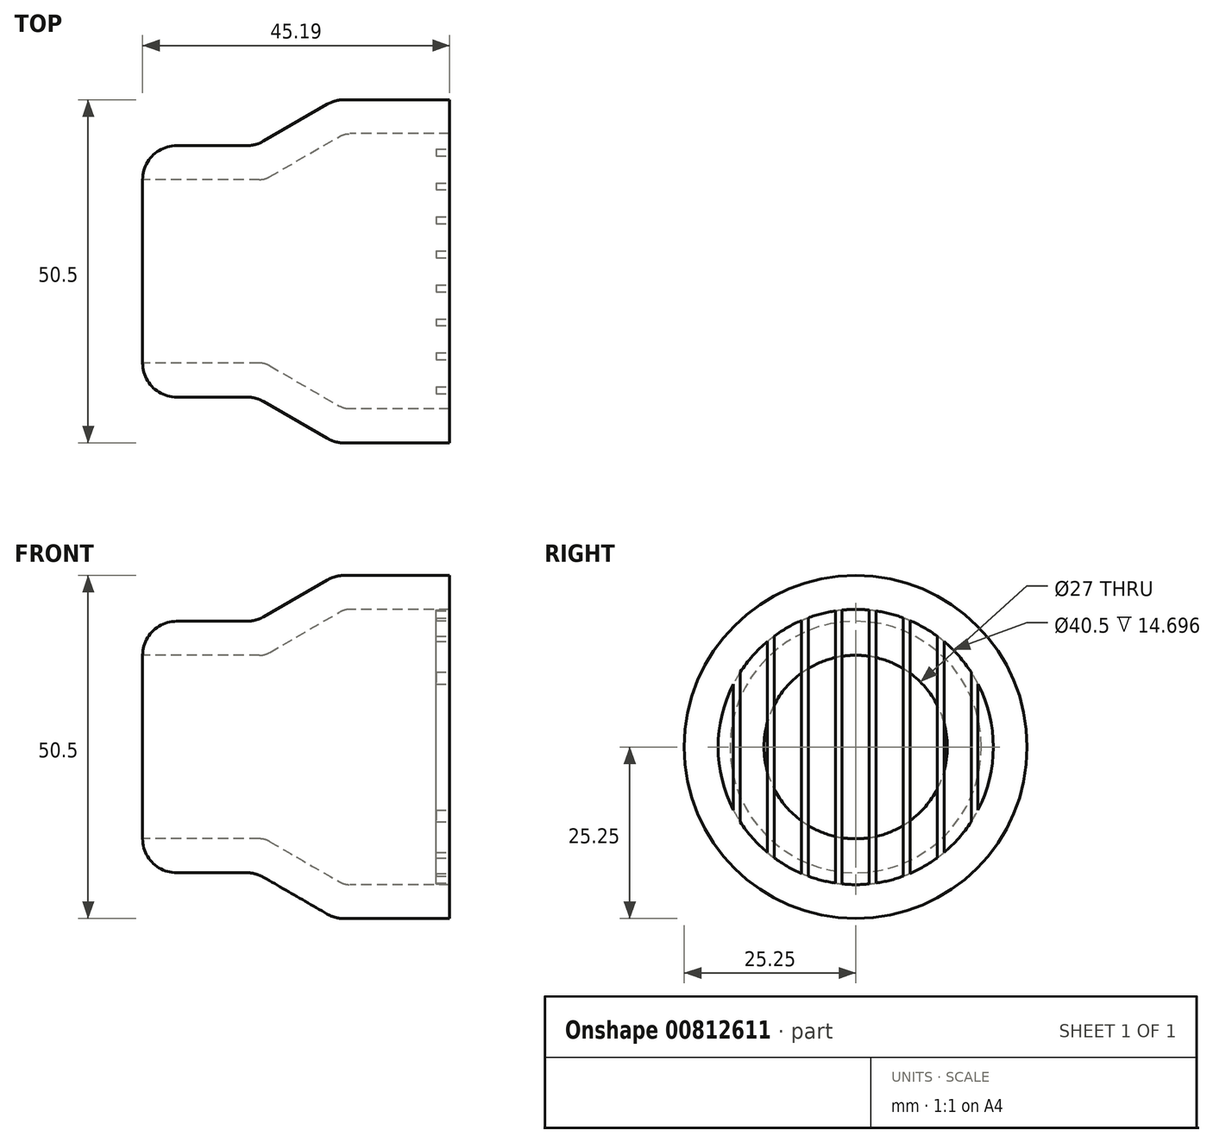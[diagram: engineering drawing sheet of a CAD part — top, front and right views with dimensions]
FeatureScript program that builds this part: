
annotation { "Feature Type Name" : "Feature", "Feature Type Description" : "" }
export const myFeature = defineFeature(function(context is Context, id is Id, definition is map)
    precondition{}
    {
        {
            var Q0;
            Q0=qCreatedBy(makeId("Top.planeOp"),FACE);
            var sketch = newSketch(context, id + "F0", { "sketchPlane" : qUnion([Q0])});
            skLineSegment(sketch, "E0", {"start": v(-18, 13.5) * mm, "end": v(0, 13.5) * mm});
            skLineSegment(sketch, "E1", {"start": v(0, 13.5) * mm, "end": v(11.7, 20.25) * mm});
            skLineSegment(sketch, "E2", {"start": v(11.7, 20.25) * mm, "end": v(25.2, 20.25) * mm});
            skLineSegment(sketch, "E3.0", {"start": v(10.35, 25.25) * mm, "end": v(25.2, 25.25) * mm});
            skLineSegment(sketch, "E3.1", {"start": v(-1.34, 18.5) * mm, "end": v(10.35, 25.25) * mm});
            skLineSegment(sketch, "E3.2", {"start": v(-18, 18.5) * mm, "end": v(-1.34, 18.5) * mm});
            skLineSegment(sketch, "E4", {"start": v(-18, 13.5) * mm, "end": v(-18, 18.5) * mm});
            skLineSegment(sketch, "E5", {"start": v(25.2, 25.25) * mm, "end": v(25.2, 20.25) * mm});
            skLineSegment(sketch, "E6", {"start": v(-63.57, 0) * mm, "end": v(46.05, 0) * mm});
            skSolve(sketch);
        }
        {
            var Q0;
            Q0=qSketchRegion(id+"F0",true);
            var Q1;
            Q1=sQuery(id+"F0.wireOp",EDGE,"E6");
            revolve(context, id + "F1", {"surfaceOperationType" : NewSurfaceOperationType.NEW, "entities" : qUnion([Q0]), "axis" : qUnion([Q1]), "revolveType" : RevolveType.FULL});
        }
        {
            var Q0;
            Q0=makeQuery(id+"F1.opRevolve","SWEPT_FACE",FACE,{"disambiguationData":[OSD([sQuery(id+"F0.wireOp",EDGE,"E5")])]});
            var sketch = newSketch(context, id + "F2", { "sketchPlane" : qUnion([Q0])});
            skCircle(sketch, "E7.0", {"center": v(0, 0) * mm, "radius": 25.25 * mm});
            skSolve(sketch);
        }
        {
            var Q0;
            Q0=qSketchRegion(id+"F2",true);
            extrude(context, id + "F3", {"entities" : qUnion([Q0]), "operationType" : NewBodyOperationType.ADD, "depth" : 2 * mm, "offsetDistance" : 25 * mm});
        }
        {
            var Q0;
            Q0=makeQuery(id+"F3.opExtrude","CAP_FACE",FACE,{"disambiguationData":[OSD([sQuery(id+"F2.wireOp",EDGE,"E7.0")])],"isStart":false});
            var sketch = newSketch(context, id + "F4", { "sketchPlane" : qUnion([Q0])});
            skLineSegment(sketch, "E8.bottom", {"start": v(-2, 64.44) * mm, "end": v(2, 64.44) * mm});
            skLineSegment(sketch, "E8.top", {"start": v(-2, -43.56) * mm, "end": v(2, -43.56) * mm});
            skLineSegment(sketch, "E8.left", {"start": v(-2, 64.44) * mm, "end": v(-2, -43.56) * mm});
            skLineSegment(sketch, "E8.right", {"start": v(2, 64.44) * mm, "end": v(2, -43.56) * mm});
            skLineSegment(sketch, "E9.1.0.0", {"start": v(3, -43.56) * mm, "end": v(7, -43.56) * mm});
            skLineSegment(sketch, "E9.1.0.1", {"start": v(7, 64.44) * mm, "end": v(7, -43.56) * mm});
            skLineSegment(sketch, "E9.1.0.2", {"start": v(3, 64.44) * mm, "end": v(3, -43.56) * mm});
            skLineSegment(sketch, "E9.1.0.3", {"start": v(3, 64.44) * mm, "end": v(7, 64.44) * mm});
            skLineSegment(sketch, "E9.2.0.0", {"start": v(8, -43.56) * mm, "end": v(12, -43.56) * mm});
            skLineSegment(sketch, "E9.2.0.1", {"start": v(12, 64.44) * mm, "end": v(12, -43.56) * mm});
            skLineSegment(sketch, "E9.2.0.2", {"start": v(8, 64.44) * mm, "end": v(8, -43.56) * mm});
            skLineSegment(sketch, "E9.2.0.3", {"start": v(8, 64.44) * mm, "end": v(12, 64.44) * mm});
            skLineSegment(sketch, "E9.3.0.0", {"start": v(13, -43.56) * mm, "end": v(17, -43.56) * mm});
            skLineSegment(sketch, "E9.3.0.1", {"start": v(17, 64.44) * mm, "end": v(17, -43.56) * mm});
            skLineSegment(sketch, "E9.3.0.2", {"start": v(13, 64.44) * mm, "end": v(13, -43.56) * mm});
            skLineSegment(sketch, "E9.3.0.3", {"start": v(13, 64.44) * mm, "end": v(17, 64.44) * mm});
            skLineSegment(sketch, "E9.4.0.0", {"start": v(18, -43.56) * mm, "end": v(22, -43.56) * mm});
            skLineSegment(sketch, "E9.4.0.1", {"start": v(22, 64.44) * mm, "end": v(22, -43.56) * mm});
            skLineSegment(sketch, "E9.4.0.2", {"start": v(18, 64.44) * mm, "end": v(18, -43.56) * mm});
            skLineSegment(sketch, "E9.4.0.3", {"start": v(18, 64.44) * mm, "end": v(22, 64.44) * mm});
            skLineSegment(sketch, "E9.5.0.0", {"start": v(23, -43.56) * mm, "end": v(27, -43.56) * mm});
            skLineSegment(sketch, "E9.5.0.1", {"start": v(27, 64.44) * mm, "end": v(27, -43.56) * mm});
            skLineSegment(sketch, "E9.5.0.2", {"start": v(23, 64.44) * mm, "end": v(23, -43.56) * mm});
            skLineSegment(sketch, "E9.5.0.3", {"start": v(23, 64.44) * mm, "end": v(27, 64.44) * mm});
            skLineSegment(sketch, "E9.direction1", {"start": v(-2, -43.56) * mm, "end": v(3, -43.56) * mm, "construction": true});
            skLineSegment(sketch, "E10.1.0.0", {"start": v(-3, 64.44) * mm, "end": v(-3, -43.56) * mm});
            skLineSegment(sketch, "E10.1.0.1", {"start": v(-7, -43.56) * mm, "end": v(-3, -43.56) * mm});
            skLineSegment(sketch, "E10.1.0.2", {"start": v(-7, 64.44) * mm, "end": v(-7, -43.56) * mm});
            skLineSegment(sketch, "E10.1.0.3", {"start": v(-7, 64.44) * mm, "end": v(-3, 64.44) * mm});
            skLineSegment(sketch, "E10.2.0.0", {"start": v(-8, 64.44) * mm, "end": v(-8, -43.56) * mm});
            skLineSegment(sketch, "E10.2.0.1", {"start": v(-12, -43.56) * mm, "end": v(-8, -43.56) * mm});
            skLineSegment(sketch, "E10.2.0.2", {"start": v(-12, 64.44) * mm, "end": v(-12, -43.56) * mm});
            skLineSegment(sketch, "E10.2.0.3", {"start": v(-12, 64.44) * mm, "end": v(-8, 64.44) * mm});
            skLineSegment(sketch, "E10.3.0.0", {"start": v(-13, 64.44) * mm, "end": v(-13, -43.56) * mm});
            skLineSegment(sketch, "E10.3.0.1", {"start": v(-17, -43.56) * mm, "end": v(-13, -43.56) * mm});
            skLineSegment(sketch, "E10.3.0.2", {"start": v(-17, 64.44) * mm, "end": v(-17, -43.56) * mm});
            skLineSegment(sketch, "E10.3.0.3", {"start": v(-17, 64.44) * mm, "end": v(-13, 64.44) * mm});
            skLineSegment(sketch, "E10.4.0.0", {"start": v(-18, 64.44) * mm, "end": v(-18, -43.56) * mm});
            skLineSegment(sketch, "E10.4.0.1", {"start": v(-22, -43.56) * mm, "end": v(-18, -43.56) * mm});
            skLineSegment(sketch, "E10.4.0.2", {"start": v(-22, 64.44) * mm, "end": v(-22, -43.56) * mm});
            skLineSegment(sketch, "E10.4.0.3", {"start": v(-22, 64.44) * mm, "end": v(-18, 64.44) * mm});
            skLineSegment(sketch, "E10.5.0.0", {"start": v(-23, 64.44) * mm, "end": v(-23, -43.56) * mm});
            skLineSegment(sketch, "E10.5.0.1", {"start": v(-27, -43.56) * mm, "end": v(-23, -43.56) * mm});
            skLineSegment(sketch, "E10.5.0.2", {"start": v(-27, 64.44) * mm, "end": v(-27, -43.56) * mm});
            skLineSegment(sketch, "E10.5.0.3", {"start": v(-27, 64.44) * mm, "end": v(-23, 64.44) * mm});
            skLineSegment(sketch, "E10.direction1", {"start": v(-2, -43.56) * mm, "end": v(-7, -43.56) * mm, "construction": true});
            skCircle(sketch, "E11.0", {"center": v(0, 0) * mm, "radius": 25.25 * mm});
            skCircle(sketch, "E12", {"center": v(0, 0) * mm, "radius": 20.25 * mm});
            skSolve(sketch);
        }
        {
            var Q0;
            {var subQ0=sQuery(id+"F4.wireOp",EDGE,"E12");var subQ1=sQuery(id+"F4.wireOp",EDGE,"E9.5.0.2");var subQ2=makeQuery(id+"F4.imprint","INTERSECT",VERTEX,{"disambiguationData":[OD(0.0)],"derivedFrom":[subQ1,subQ0]});Q0=makeQuery(id+"F4.imprint","IMPRINT",FACE,{"disambiguationData":[TD([[makeQuery(id+"F4.imprint","IMPRINT",EDGE,{"disambiguationData":[TD([[subQ2,-1.0]])],"derivedFrom":subQ1}),1.0]])]});}
            var Q1;
            {var subQ0=sQuery(id+"F4.wireOp",EDGE,"E12");var subQ1=sQuery(id+"F4.wireOp",EDGE,"E9.4.0.1");var subQ2=makeQuery(id+"F4.imprint","INTERSECT",VERTEX,{"disambiguationData":[OD(0.0)],"derivedFrom":[subQ1,subQ0]});Q1=makeQuery(id+"F4.imprint","IMPRINT",FACE,{"disambiguationData":[TD([[makeQuery(id+"F4.imprint","IMPRINT",EDGE,{"disambiguationData":[TD([[subQ2,-1.0]])],"derivedFrom":subQ1}),-1.0]])]});}
            var Q2;
            {var subQ0=sQuery(id+"F4.wireOp",EDGE,"E12");var subQ1=sQuery(id+"F4.wireOp",EDGE,"E9.3.0.1");var subQ2=makeQuery(id+"F4.imprint","INTERSECT",VERTEX,{"disambiguationData":[OD(0.0)],"derivedFrom":[subQ1,subQ0]});Q2=makeQuery(id+"F4.imprint","IMPRINT",FACE,{"disambiguationData":[TD([[makeQuery(id+"F4.imprint","IMPRINT",EDGE,{"disambiguationData":[TD([[subQ2,-1.0]])],"derivedFrom":subQ1}),-1.0]])]});}
            var Q3;
            {var subQ0=sQuery(id+"F4.wireOp",EDGE,"E12");var subQ1=sQuery(id+"F4.wireOp",EDGE,"E9.2.0.1");var subQ2=makeQuery(id+"F4.imprint","INTERSECT",VERTEX,{"disambiguationData":[OD(0.0)],"derivedFrom":[subQ1,subQ0]});Q3=makeQuery(id+"F4.imprint","IMPRINT",FACE,{"disambiguationData":[TD([[makeQuery(id+"F4.imprint","IMPRINT",EDGE,{"disambiguationData":[TD([[subQ2,-1.0]])],"derivedFrom":subQ1}),-1.0]])]});}
            var Q4;
            {var subQ0=sQuery(id+"F4.wireOp",EDGE,"E12");var subQ1=sQuery(id+"F4.wireOp",EDGE,"E9.1.0.1");var subQ2=makeQuery(id+"F4.imprint","INTERSECT",VERTEX,{"disambiguationData":[OD(0.0)],"derivedFrom":[subQ1,subQ0]});Q4=makeQuery(id+"F4.imprint","IMPRINT",FACE,{"disambiguationData":[TD([[makeQuery(id+"F4.imprint","IMPRINT",EDGE,{"disambiguationData":[TD([[subQ2,-1.0]])],"derivedFrom":subQ1}),-1.0]])]});}
            var Q5;
            {var subQ0=sQuery(id+"F4.wireOp",EDGE,"E12");var subQ1=sQuery(id+"F4.wireOp",EDGE,"E8.left");var subQ2=makeQuery(id+"F4.imprint","INTERSECT",VERTEX,{"disambiguationData":[OD(0.0)],"derivedFrom":[subQ1,subQ0]});Q5=makeQuery(id+"F4.imprint","IMPRINT",FACE,{"disambiguationData":[TD([[makeQuery(id+"F4.imprint","IMPRINT",EDGE,{"disambiguationData":[TD([[subQ2,-1.0]])],"derivedFrom":subQ1}),1.0]])]});}
            var Q6;
            {var subQ0=sQuery(id+"F4.wireOp",EDGE,"E12");var subQ1=sQuery(id+"F4.wireOp",EDGE,"E10.1.0.0");var subQ2=makeQuery(id+"F4.imprint","INTERSECT",VERTEX,{"disambiguationData":[OD(0.0)],"derivedFrom":[subQ1,subQ0]});Q6=makeQuery(id+"F4.imprint","IMPRINT",FACE,{"disambiguationData":[TD([[makeQuery(id+"F4.imprint","IMPRINT",EDGE,{"disambiguationData":[TD([[subQ2,-1.0]])],"derivedFrom":subQ1}),-1.0]])]});}
            var Q7;
            {var subQ0=sQuery(id+"F4.wireOp",EDGE,"E12");var subQ1=sQuery(id+"F4.wireOp",EDGE,"E10.2.0.0");var subQ2=makeQuery(id+"F4.imprint","INTERSECT",VERTEX,{"disambiguationData":[OD(0.0)],"derivedFrom":[subQ1,subQ0]});Q7=makeQuery(id+"F4.imprint","IMPRINT",FACE,{"disambiguationData":[TD([[makeQuery(id+"F4.imprint","IMPRINT",EDGE,{"disambiguationData":[TD([[subQ2,-1.0]])],"derivedFrom":subQ1}),-1.0]])]});}
            var Q8;
            {var subQ0=sQuery(id+"F4.wireOp",EDGE,"E12");var subQ1=sQuery(id+"F4.wireOp",EDGE,"E10.3.0.0");var subQ2=makeQuery(id+"F4.imprint","INTERSECT",VERTEX,{"disambiguationData":[OD(0.0)],"derivedFrom":[subQ1,subQ0]});Q8=makeQuery(id+"F4.imprint","IMPRINT",FACE,{"disambiguationData":[TD([[makeQuery(id+"F4.imprint","IMPRINT",EDGE,{"disambiguationData":[TD([[subQ2,-1.0]])],"derivedFrom":subQ1}),-1.0]])]});}
            var Q9;
            {var subQ0=sQuery(id+"F4.wireOp",EDGE,"E12");var subQ1=sQuery(id+"F4.wireOp",EDGE,"E10.4.0.0");var subQ2=makeQuery(id+"F4.imprint","INTERSECT",VERTEX,{"disambiguationData":[OD(0.0)],"derivedFrom":[subQ1,subQ0]});Q9=makeQuery(id+"F4.imprint","IMPRINT",FACE,{"disambiguationData":[TD([[makeQuery(id+"F4.imprint","IMPRINT",EDGE,{"disambiguationData":[TD([[subQ2,-1.0]])],"derivedFrom":subQ1}),-1.0]])]});}
            var Q10;
            {var subQ0=sQuery(id+"F4.wireOp",EDGE,"E12");var subQ1=sQuery(id+"F4.wireOp",EDGE,"E10.5.0.0");var subQ2=makeQuery(id+"F4.imprint","INTERSECT",VERTEX,{"disambiguationData":[OD(0.0)],"derivedFrom":[subQ1,subQ0]});Q10=makeQuery(id+"F4.imprint","IMPRINT",FACE,{"disambiguationData":[TD([[makeQuery(id+"F4.imprint","IMPRINT",EDGE,{"disambiguationData":[TD([[subQ2,-1.0]])],"derivedFrom":subQ1}),-1.0]])]});}
            var Q11;
            {var subQ0=sQuery(id+"F4.wireOp",EDGE,"E12");var subQ1=sQuery(id+"F4.wireOp",EDGE,"E9.3.0.2");var subQ2=makeQuery(id+"F4.imprint","INTERSECT",VERTEX,{"disambiguationData":[OD(0.0)],"derivedFrom":[subQ1,subQ0]});Q11=makeQuery(id+"F4.imprint","IMPRINT",FACE,{"disambiguationData":[TD([[makeQuery(id+"F4.imprint","IMPRINT",EDGE,{"disambiguationData":[TD([[subQ2,-1.0]])],"derivedFrom":subQ1}),1.0]])]});}
            var Q12;
            {var subQ0=sQuery(id+"F4.wireOp",EDGE,"E12");var subQ1=sQuery(id+"F4.wireOp",EDGE,"E9.4.0.2");var subQ2=makeQuery(id+"F4.imprint","INTERSECT",VERTEX,{"disambiguationData":[OD(0.0)],"derivedFrom":[subQ1,subQ0]});Q12=makeQuery(id+"F4.imprint","IMPRINT",FACE,{"disambiguationData":[TD([[makeQuery(id+"F4.imprint","IMPRINT",EDGE,{"disambiguationData":[TD([[subQ2,-1.0]])],"derivedFrom":subQ1}),1.0]])]});}
            var Q13;
            Q13=makeQuery(id+"F3.opExtrude","CAP_FACE",FACE,{"disambiguationData":[OSD([sQuery(id+"F2.wireOp",EDGE,"E7.0")])],"isStart":true});
            extrude(context, id + "F5", {"entities" : qUnion([Q0, Q1, Q2, Q3, Q4, Q5, Q6, Q7, Q8, Q9, Q10, Q11, Q12]), "operationType" : NewBodyOperationType.REMOVE, "endBound" : BoundingType.UP_TO_SURFACE, "oppositeDirection" : true, "depth" : 25 * mm, "endBoundEntityFace" : qUnion([Q13]), "offsetDistance" : 25 * mm});
        }
        {
            var Q0;
            Q0=makeQuery(id+"F1.opRevolve","SWEPT_EDGE",EDGE,{"disambiguationData":[OSD([sQuery(id+"F0.wireOp",EDGE,"E3.2"),sQuery(id+"F0.wireOp",EDGE,"E4")])]});
            var Q1;
            Q1=makeQuery(id+"F1.opRevolve","SWEPT_EDGE",EDGE,{"disambiguationData":[OSD([sQuery(id+"F0.wireOp",EDGE,"E3.1"),sQuery(id+"F0.wireOp",EDGE,"E3.2")])]});
            var Q2;
            Q2=makeQuery(id+"F1.opRevolve","SWEPT_EDGE",EDGE,{"disambiguationData":[OSD([sQuery(id+"F0.wireOp",EDGE,"E3.0"),sQuery(id+"F0.wireOp",EDGE,"E3.1")])]});
            fillet(context, id + "F6", {"entities" : qUnion([Q0, Q1, Q2]), "radius" : 5 * mm, "tangentPropagation" : true, "allowEdgeOverflow" : false});
        }
        {
            var Q0;
            Q0=makeQuery(id+"F1.opRevolve","SWEPT_EDGE",EDGE,{"disambiguationData":[OSD([sQuery(id+"F0.wireOp",EDGE,"E1"),sQuery(id+"F0.wireOp",EDGE,"E2")])]});
            var Q1;
            Q1=makeQuery(id+"F1.opRevolve","SWEPT_EDGE",EDGE,{"disambiguationData":[OSD([sQuery(id+"F0.wireOp",EDGE,"E0"),sQuery(id+"F0.wireOp",EDGE,"E1")])]});
            fillet(context, id + "F7", {"entities" : qUnion([Q0, Q1]), "radius" : 3 * mm, "tangentPropagation" : true, "allowEdgeOverflow" : false});
        }
    });
